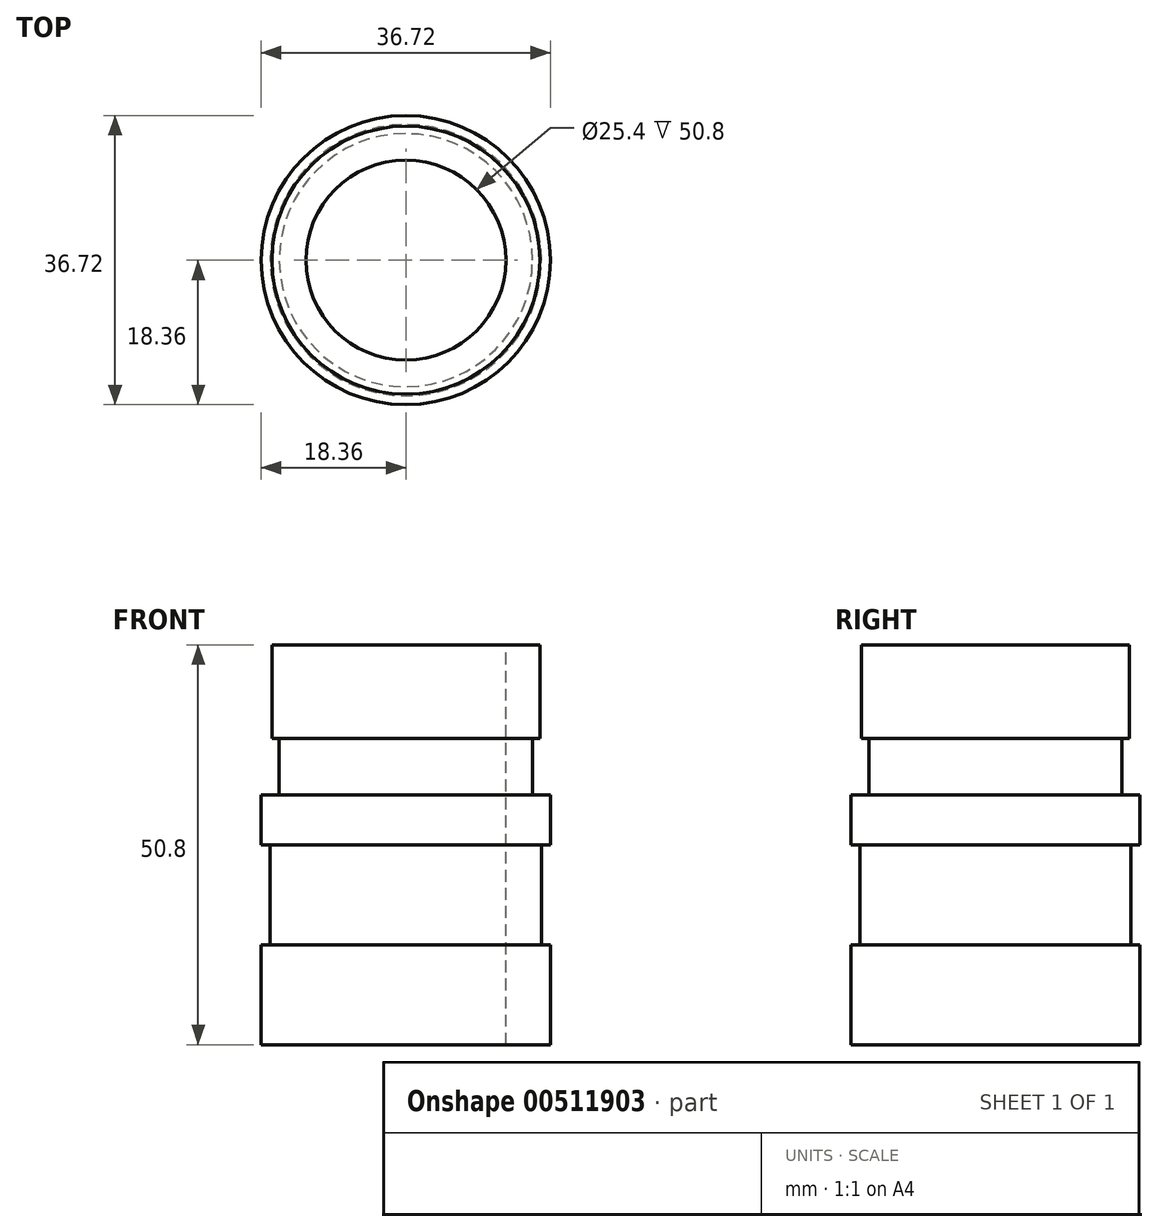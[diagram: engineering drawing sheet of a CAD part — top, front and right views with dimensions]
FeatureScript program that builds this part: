
annotation { "Feature Type Name" : "Feature", "Feature Type Description" : "" }
export const myFeature = defineFeature(function(context is Context, id is Id, definition is map)
    precondition{}
    {
        {
            var Q0;
            Q0=qCreatedBy(makeId("Front.planeOp"),FACE);
            var sketch = newSketch(context, id + "F0", { "sketchPlane" : qUnion([Q0])});
            skLineSegment(sketch, "E0", {"start": v(0, 11.12) * mm, "end": v(0, 0) * mm});
            skSolve(sketch);
        }
        {
            var Q0;
            Q0=qCreatedBy(makeId("Front.planeOp"),FACE);
            var sketch = newSketch(context, id + "F1", { "sketchPlane" : qUnion([Q0])});
            skLineSegment(sketch, "E1", {"start": v(12.7, 50.8) * mm, "end": v(12.7, 0) * mm});
            skLineSegment(sketch, "E2", {"start": v(12.7, 0) * mm, "end": v(18.36, 0) * mm});
            skLineSegment(sketch, "E3", {"start": v(18.36, 0) * mm, "end": v(18.36, 12.7) * mm});
            skLineSegment(sketch, "E4", {"start": v(17.02, 50.8) * mm, "end": v(12.7, 50.8) * mm});
            skLineSegment(sketch, "E5", {"start": v(17.02, 38.88) * mm, "end": v(16.08, 38.88) * mm});
            skLineSegment(sketch, "E6", {"start": v(16.08, 38.88) * mm, "end": v(16.08, 31.75) * mm});
            skLineSegment(sketch, "E7", {"start": v(16.08, 31.75) * mm, "end": v(18.36, 31.75) * mm});
            skLineSegment(sketch, "E8", {"start": v(18.36, 31.75) * mm, "end": v(18.36, 25.4) * mm});
            skLineSegment(sketch, "E9", {"start": v(18.36, 25.4) * mm, "end": v(17.22, 25.4) * mm});
            skLineSegment(sketch, "E10", {"start": v(17.22, 12.7) * mm, "end": v(18.36, 12.7) * mm});
            skLineSegment(sketch, "E11.trimOffspring", {"start": v(18.36, 25.4) * mm, "end": v(18.36, 31.75) * mm});
            skLineSegment(sketch, "E12", {"start": v(17.22, 25.4) * mm, "end": v(17.22, 12.7) * mm});
            skLineSegment(sketch, "E13", {"start": v(17.02, 38.88) * mm, "end": v(17.02, 50.8) * mm});
            skSolve(sketch);
        }
        {
            var Q0;
            Q0=makeQuery(id+"F1.imprint","IMPRINT",FACE,{"disambiguationData":[TD([[makeQuery(id+"F1.imprint","IMPRINT",EDGE,{"derivedFrom":sQuery(id+"F1.wireOp",EDGE,"E1")}),1.0]])]});
            var Q1;
            Q1=sQuery(id+"F0.wireOp",EDGE,"E0");
            revolve(context, id + "F2", {"entities" : qUnion([Q0]), "axis" : qUnion([Q1]), "revolveType" : RevolveType.FULL});
        }
    });
